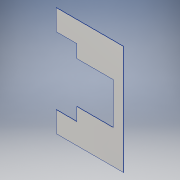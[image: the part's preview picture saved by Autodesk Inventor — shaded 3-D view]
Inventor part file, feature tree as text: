
AUTODESK INVENTOR PART (.ipt)
format: ipt  version: 2016 (Build 200138000, 138)  size: 105,472 bytes
history: native  units: in
note: dims shown in document units (in); Inventor stores cm internally (conversion verified against a paired STEP export)
features: extrude x1, sketch x1
ambient origin geometry x8: Origin, YZ Plane, XZ Plane, XY Plane, X Axis, Y Axis, Z Axis, Center Point
bodies: Solid1 (feature_tree)
feature tree (2):
  extrude  "Extrusion1"  Depth=14.0in
  sketch  "Sketch1"  dims[d2=0.0625in d3=0.0in d4=14.0in d5=4.0in d6=4.0in d7=17.0in d9=2.5in d10=2.5in d11=2.0in d12=4.0in]
